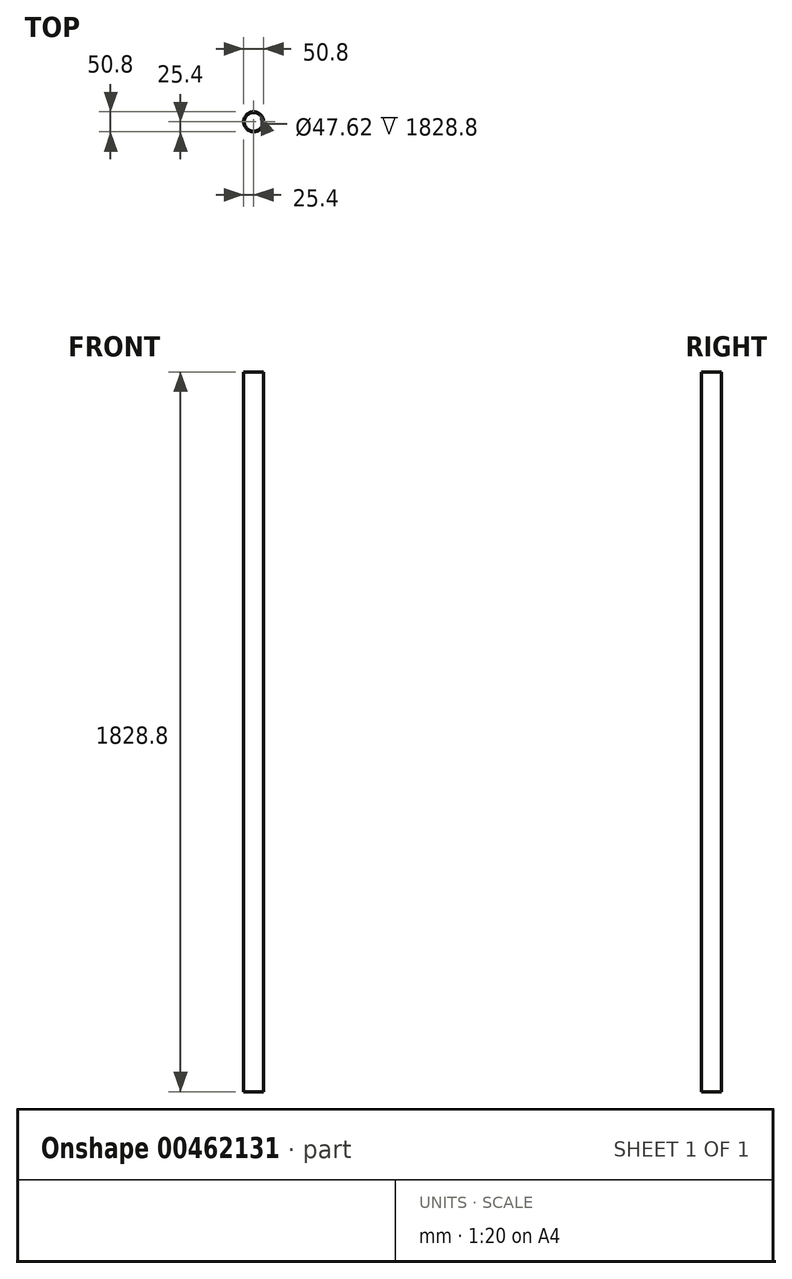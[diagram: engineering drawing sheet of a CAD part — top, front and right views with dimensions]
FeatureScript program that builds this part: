
annotation { "Feature Type Name" : "Feature", "Feature Type Description" : "" }
export const myFeature = defineFeature(function(context is Context, id is Id, definition is map)
    precondition{}
    {
        {
            var Q0;
            Q0=qCreatedBy(makeId("Top.planeOp"),FACE);
            var sketch = newSketch(context, id + "F0", { "sketchPlane" : qUnion([Q0])});
            skLineSegment(sketch, "E0", {"start": v(0, 0) * mm, "end": v(0, 578.97) * mm, "construction": true});
            skCircle(sketch, "E1", {"center": v(0, 254) * mm, "radius": 25.4 * mm});
            skCircle(sketch, "E2", {"center": v(0, 254) * mm, "radius": 23.81 * mm});
            skSolve(sketch);
        }
        {
            var Q0;
            Q0 = qSketchRegion(id + "F0", true);
            extrude(context, id + "F1", {"entities" : qUnion([Q0]), "depth" : 1828.8 * mm});
        }
    });
